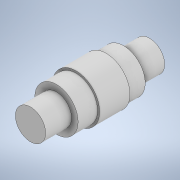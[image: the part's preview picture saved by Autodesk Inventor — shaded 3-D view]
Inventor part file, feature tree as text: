
AUTODESK INVENTOR PART (.ipt)
format: ipt  version: 2020.3 (Build 243373000, 373)  size: 126,976 bytes
history: native  units: mm
features: extrude x5, sketch x5
ambient origin geometry x8: Origin, YZ Plane, XZ Plane, XY Plane, X Axis, Y Axis, Z Axis, Center Point
bodies: Solid1 (feature_tree)
feature tree (10):
  extrude  "Extrusion1"  Depth=12.0mm TaperAngle=0.0deg
  extrude  "Extrusion2"  Depth=8.0mm TaperAngle=0.0deg
  extrude  "Extrusion3"  Depth=9.0mm TaperAngle=0.0deg
  extrude  "Extrusion4"  Depth=12.0mm TaperAngle=0.0deg
  extrude  "Extrusion5"  [1 undecoded]
  sketch  "Sketch1"  dims[d0=14.0mm d1=12.0mm d2=0.0mm]
  sketch  "Sketch2"  dims[d3=20.0mm d4=8.0mm d5=0.0mm]
  sketch  "Sketch3"  dims[d6=14.0mm d7=0.0mm d8=9.0mm d9=0.0mm]
  sketch  "Sketch4"  dims[d10=14.0mm d11=12.0mm d12=0.0mm]
  sketch  "Sketch5"
note: 1 required parameter value undecoded (feature->parameter linkage not recoverable at this tier; creation-order binding heuristic only, values carry confidence <= 0.55)
